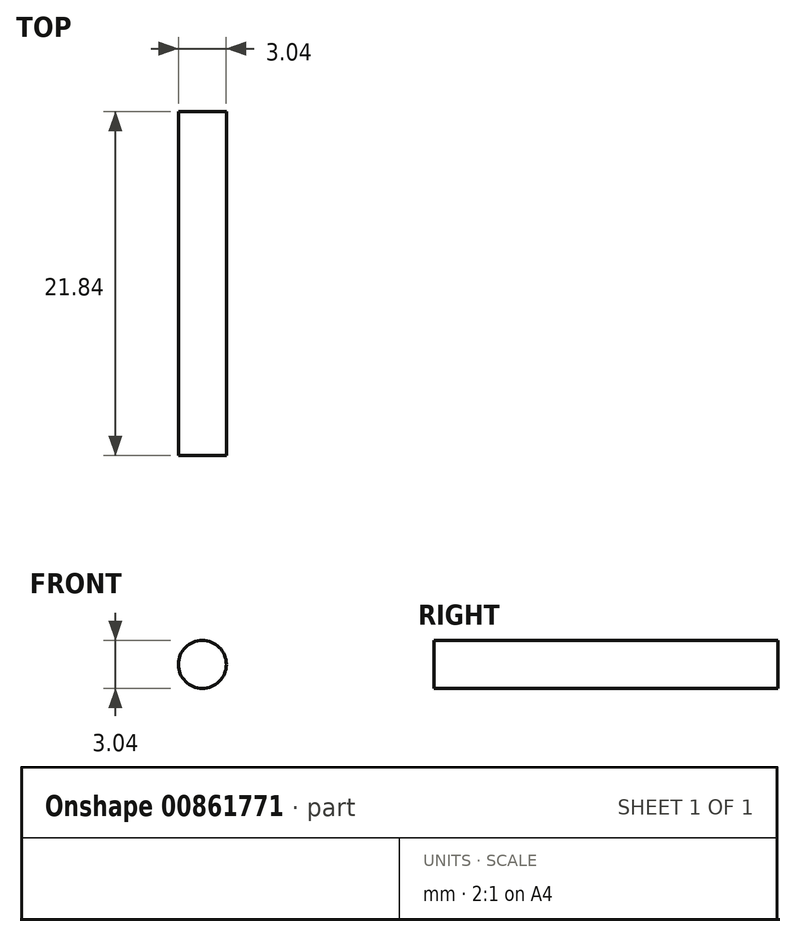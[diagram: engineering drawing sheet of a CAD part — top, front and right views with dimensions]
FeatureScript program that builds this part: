
annotation { "Feature Type Name" : "Feature", "Feature Type Description" : "" }
export const myFeature = defineFeature(function(context is Context, id is Id, definition is map)
    precondition{}
    {
        {
            var Q0;
            Q0=qCreatedBy(makeId("Front.planeOp"),FACE);
            var sketch = newSketch(context, id + "F0", { "sketchPlane" : qUnion([Q0])});
            skCircle(sketch, "E0", {"center": v(0, 0) * mm, "radius": 1.52 * mm});
            skSolve(sketch);
        }
        {
            var Q0;
            Q0 = qSketchRegion(id + "F0", true);
            extrude(context, id + "F1", {"entities" : qUnion([Q0]), "depth" : 21.84 * mm, "offsetDistance" : 25.4 * mm, "symmetric" : true});
        }
    });
